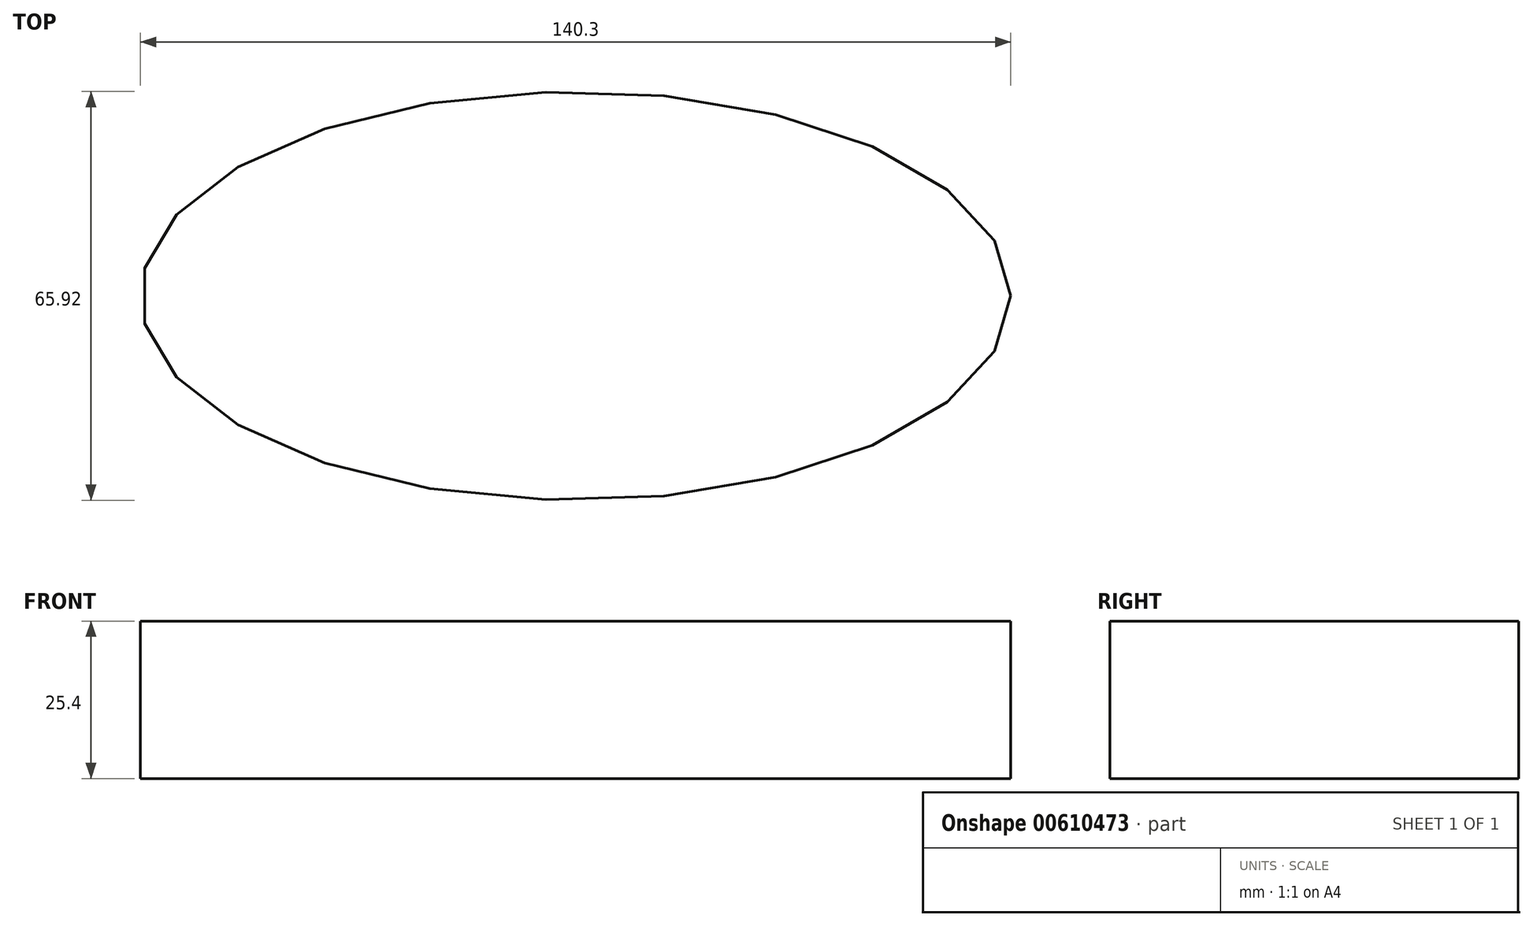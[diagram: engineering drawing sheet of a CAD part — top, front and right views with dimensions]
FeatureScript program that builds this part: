
annotation { "Feature Type Name" : "Feature", "Feature Type Description" : "" }
export const myFeature = defineFeature(function(context is Context, id is Id, definition is map)
    precondition{}
    {
        {
            var Q0;
            Q0=qCreatedBy(makeId("Top.planeOp"),FACE);
            var sketch = newSketch(context, id + "F0", { "sketchPlane" : qUnion([Q0])});
            skEllipse(sketch, "E0", {"center": v(0, 0) * mm, "majorRadius": 70.15 * mm, "minorRadius": 32.96 * mm, "majorAxis": v(1, 0)});
            skSolve(sketch);
        }
        {
            var Q0;
            Q0=makeQuery(id+"F0.imprint","IMPRINT",FACE,{"disambiguationData":[TD([[makeQuery(id+"F0.imprint","IMPRINT",EDGE,{"derivedFrom":sQuery(id+"F0.wireOp",EDGE,"E0")}),1.0]])]});
            var Q1;
            Q1=sQuery(id+"F0.wireOp",EDGE,"E0");
            extrude(context, id + "F1", {"entities" : qUnion([Q0]), "surfaceEntities" : qUnion([Q1]), "depth" : 25.4 * mm, "offsetDistance" : 25.4 * mm});
        }
    });
